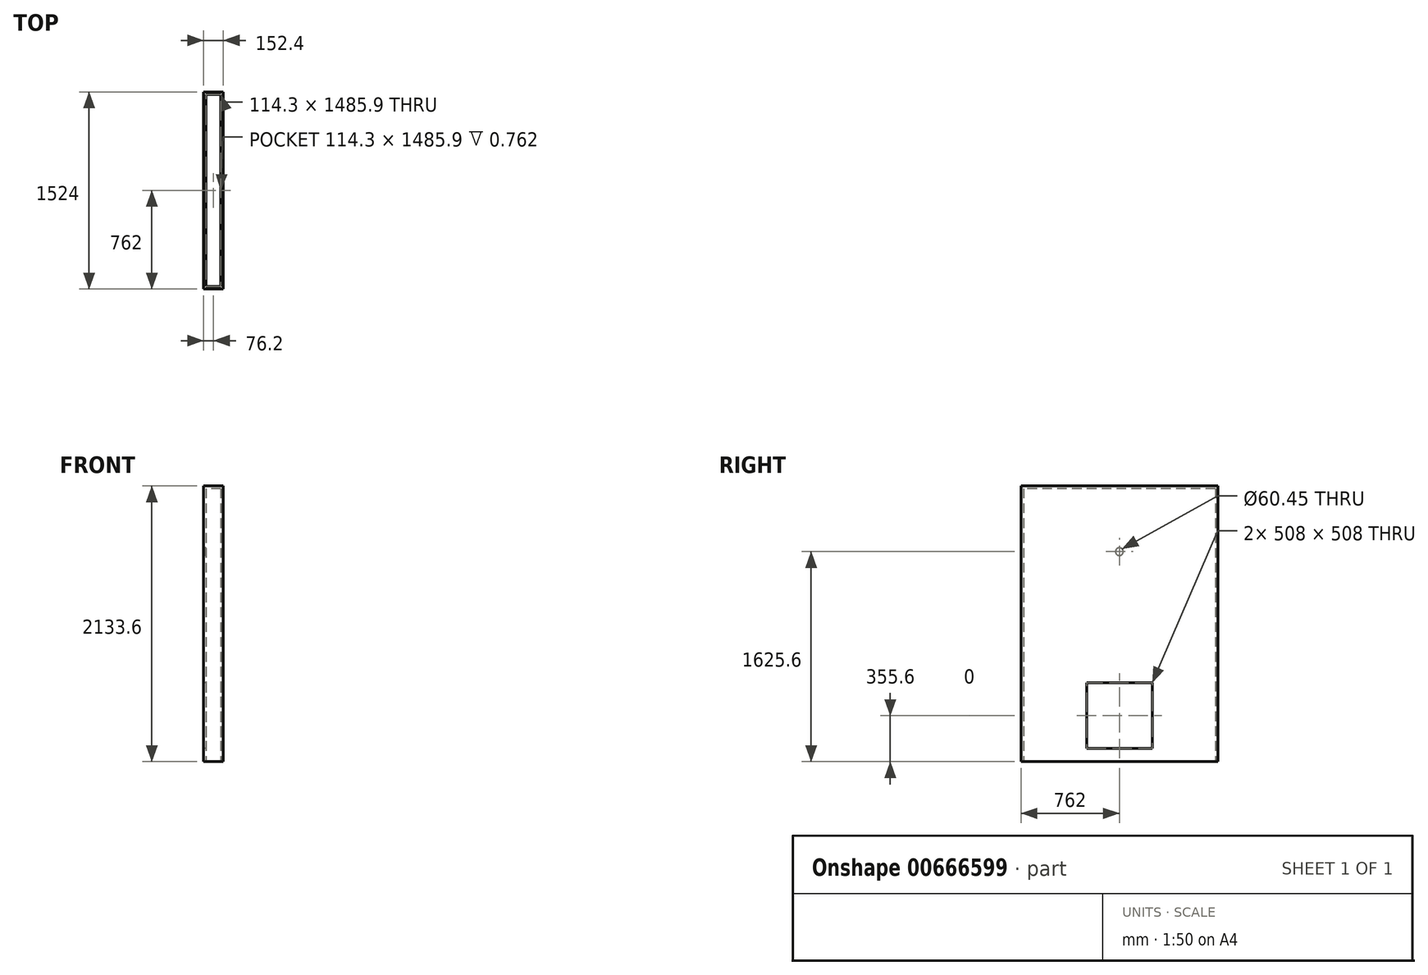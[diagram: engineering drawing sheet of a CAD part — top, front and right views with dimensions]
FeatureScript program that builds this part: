
annotation { "Feature Type Name" : "Feature", "Feature Type Description" : "" }
export const myFeature = defineFeature(function(context is Context, id is Id, definition is map)
    precondition{}
    {
        {
            var Q0;
            Q0=qCreatedBy(makeId("Top.planeOp"),FACE);
            var sketch = newSketch(context, id + "F0", { "sketchPlane" : qUnion([Q0])});
            skLineSegment(sketch, "E0.bottom", {"start": v(76.2, 762) * mm, "end": v(-76.2, 762) * mm});
            skLineSegment(sketch, "E0.top", {"start": v(76.2, -762) * mm, "end": v(-76.2, -762) * mm});
            skLineSegment(sketch, "E0.left", {"start": v(76.2, 762) * mm, "end": v(76.2, -762) * mm});
            skLineSegment(sketch, "E0.right", {"start": v(-76.2, 762) * mm, "end": v(-76.2, -762) * mm});
            skPoint(sketch, "E0.middle", {"position": v(0, 0) * mm});
            skLineSegment(sketch, "E1.bottom", {"start": v(57.15, 742.95) * mm, "end": v(-57.15, 742.95) * mm});
            skLineSegment(sketch, "E1.top", {"start": v(57.15, -742.95) * mm, "end": v(-57.15, -742.95) * mm});
            skLineSegment(sketch, "E1.left", {"start": v(57.15, 742.95) * mm, "end": v(57.15, -742.95) * mm});
            skLineSegment(sketch, "E1.right", {"start": v(-57.15, 742.95) * mm, "end": v(-57.15, -742.95) * mm});
            skSolve(sketch);
        }
        {
            var Q0;
            Q0=makeQuery(id+"F0.imprint","IMPRINT",FACE,{"disambiguationData":[TD([[makeQuery(id+"F0.imprint","IMPRINT",EDGE,{"derivedFrom":sQuery(id+"F0.wireOp",EDGE,"E0.bottom")}),1.0]])]});
            extrude(context, id + "F1", {"entities" : qUnion([Q0]), "depth" : 2133.6 * mm, "offsetDistance" : 25.4 * mm});
        }
        {
            var Q0;
            Q0=makeQuery(id+"F1.opExtrude","SWEPT_FACE",FACE,{"disambiguationData":[OSD([sQuery(id+"F0.wireOp",EDGE,"E1.top")])]});
            var sketch = newSketch(context, id + "F2", { "sketchPlane" : qUnion([Q0])});
            skLineSegment(sketch, "E2", {"start": v(-57.15, 2133.6) * mm, "end": v(-57.15, 2132.84) * mm});
            skLineSegment(sketch, "E3.bottom", {"start": v(-57.15, 2132.84) * mm, "end": v(57.15, 2132.84) * mm});
            skLineSegment(sketch, "E3.top", {"start": v(-57.15, 2113.79) * mm, "end": v(57.15, 2113.79) * mm});
            skLineSegment(sketch, "E3.left", {"start": v(-57.15, 2132.84) * mm, "end": v(-57.15, 2113.79) * mm});
            skLineSegment(sketch, "E3.right", {"start": v(57.15, 2132.84) * mm, "end": v(57.15, 2113.79) * mm});
            skSolve(sketch);
        }
        {
            var Q0;
            Q0=makeQuery(id+"F2.imprint","IMPRINT",FACE,{"disambiguationData":[TD([[makeQuery(id+"F2.imprint","IMPRINT",EDGE,{"derivedFrom":sQuery(id+"F2.wireOp",EDGE,"E3.bottom")}),-1.0]])]});
            extrude(context, id + "F3", {"entities" : qUnion([Q0]), "operationType" : NewBodyOperationType.ADD, "depth" : 1485.9 * mm, "offsetDistance" : 25.4 * mm});
        }
        {
            var Q0;
            Q0=makeQuery(id+"F1.opExtrude","SWEPT_FACE",FACE,{"disambiguationData":[OSD([sQuery(id+"F0.wireOp",EDGE,"E0.right")])]});
            var sketch = newSketch(context, id + "F4", { "sketchPlane" : qUnion([Q0])});
            skLineSegment(sketch, "E4", {"start": v(0, 2133.6) * mm, "end": v(0, 1625.6) * mm});
            skCircle(sketch, "E5", {"center": v(0, 1625.6) * mm, "radius": 30.23 * mm});
            skSolve(sketch);
        }
        {
            var Q0;
            Q0=makeQuery(id+"F4.imprint","IMPRINT",FACE,{"disambiguationData":[TD([[makeQuery(id+"F4.imprint","IMPRINT",EDGE,{"derivedFrom":sQuery(id+"F4.wireOp",EDGE,"E5")}),1.0]])]});
            extrude(context, id + "F5", {"entities" : qUnion([Q0]), "operationType" : NewBodyOperationType.REMOVE, "oppositeDirection" : true, "depth" : 25.4 * mm, "offsetDistance" : 25.4 * mm});
        }
        {
            var Q0;
            Q0=makeQuery(id+"F1.opExtrude","SWEPT_FACE",FACE,{"disambiguationData":[OSD([sQuery(id+"F0.wireOp",EDGE,"E0.right")])]});
            var sketch = newSketch(context, id + "F6", { "sketchPlane" : qUnion([Q0])});
            skLineSegment(sketch, "E6", {"start": v(0, 0) * mm, "end": v(0, 101.6) * mm});
            skLineSegment(sketch, "E7", {"start": v(0, 101.6) * mm, "end": v(0, 355.6) * mm});
            skLineSegment(sketch, "E8.bottom", {"start": v(254, 101.6) * mm, "end": v(-254, 101.6) * mm});
            skLineSegment(sketch, "E8.top", {"start": v(254, 609.6) * mm, "end": v(-254, 609.6) * mm});
            skLineSegment(sketch, "E8.left", {"start": v(254, 101.6) * mm, "end": v(254, 609.6) * mm});
            skLineSegment(sketch, "E8.right", {"start": v(-254, 101.6) * mm, "end": v(-254, 609.6) * mm});
            skPoint(sketch, "E8.middle", {"position": v(0, 355.6) * mm});
            skSolve(sketch);
        }
        {
            var Q0;
            Q0=makeQuery(id+"F6.imprint","IMPRINT",FACE,{"disambiguationData":[TD([[makeQuery(id+"F6.imprint","IMPRINT",EDGE,{"derivedFrom":sQuery(id+"F6.wireOp",EDGE,"E8.top")}),1.0]])]});
            extrude(context, id + "F7", {"entities" : qUnion([Q0]), "operationType" : NewBodyOperationType.REMOVE, "oppositeDirection" : true, "depth" : 177.8 * mm, "offsetDistance" : 25.4 * mm});
        }
    });
